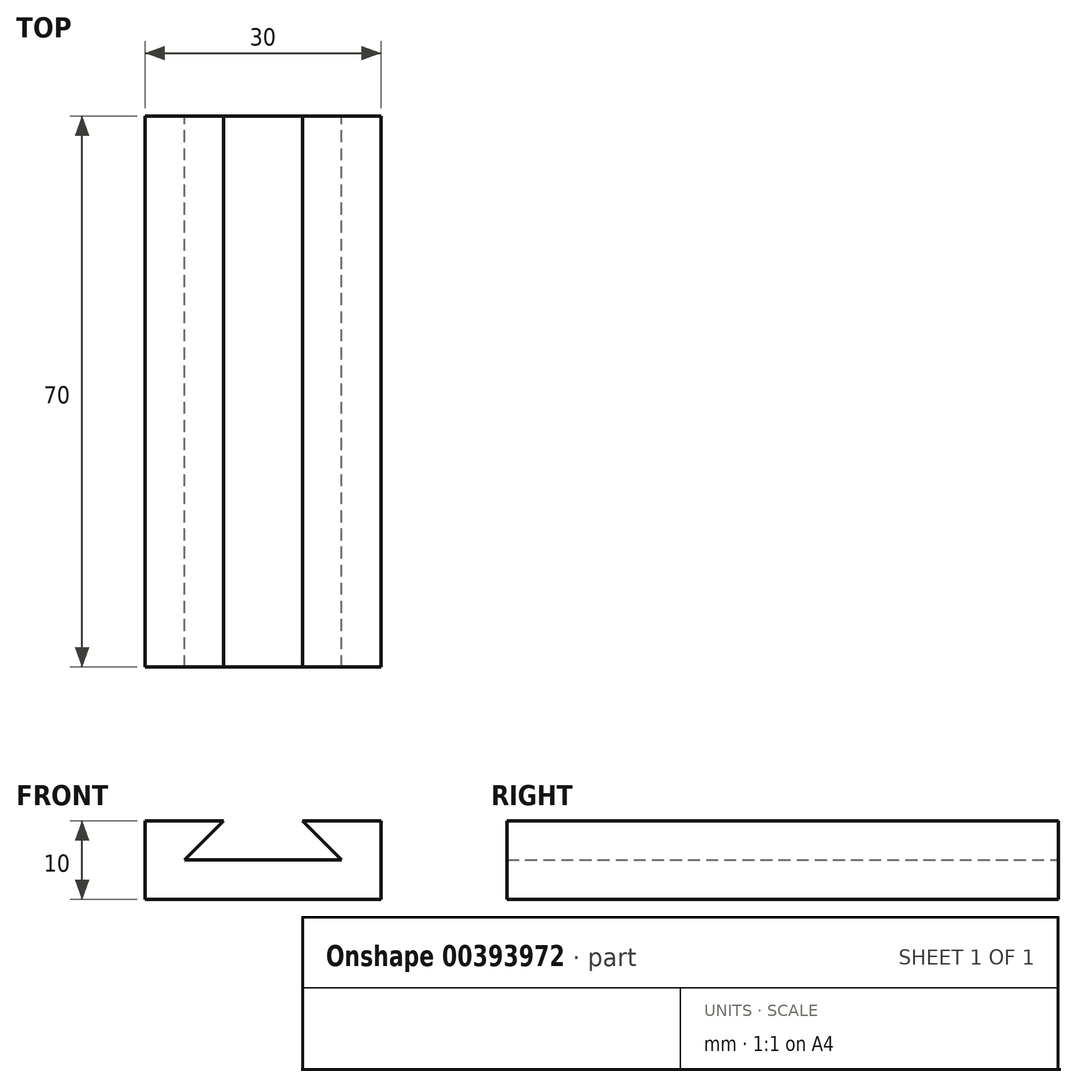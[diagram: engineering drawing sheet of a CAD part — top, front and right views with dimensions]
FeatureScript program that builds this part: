
annotation { "Feature Type Name" : "Feature", "Feature Type Description" : "" }
export const myFeature = defineFeature(function(context is Context, id is Id, definition is map)
    precondition{}
    {
        {
            var Q0;
            Q0=qCreatedBy(makeId("Front.planeOp"),FACE);
            var sketch = newSketch(context, id + "F0", { "sketchPlane" : qUnion([Q0])});
            skLineSegment(sketch, "E0.bottom", {"start": v(0, 0) * mm, "end": v(30, 0) * mm});
            skLineSegment(sketch, "E0.top", {"start": v(0, 10) * mm, "end": v(30, 10) * mm});
            skLineSegment(sketch, "E0.left", {"start": v(0, 0) * mm, "end": v(0, 10) * mm});
            skLineSegment(sketch, "E0.right", {"start": v(30, 0) * mm, "end": v(30, 10) * mm});
            skLineSegment(sketch, "E1", {"start": v(10, 10) * mm, "end": v(5, 5) * mm});
            skLineSegment(sketch, "E2", {"start": v(5, 5) * mm, "end": v(20, 5) * mm});
            skLineSegment(sketch, "E3", {"start": v(20, 5) * mm, "end": v(20, 10) * mm});
            skLineSegment(sketch, "E4", {"start": v(15, 5) * mm, "end": v(15, 10) * mm});
            skPoint(sketch, "E4.startSnap0", {"position": v(15, 0) * mm});
            skLineSegment(sketch, "E5.MirrorCS", {"start": v(20, 10) * mm, "end": v(25, 5) * mm});
            skLineSegment(sketch, "E6", {"start": v(20, 5) * mm, "end": v(25, 5) * mm});
            skSolve(sketch);
        }
        {
            var Q0;
            Q0=makeQuery(id+"F0.imprint","IMPRINT",FACE,{"disambiguationData":[TD([[makeQuery(id+"F0.imprint","IMPRINT",EDGE,{"derivedFrom":sQuery(id+"F0.wireOp",EDGE,"E0.bottom")}),1.0]])]});
            extrude(context, id + "F1", {"entities" : qUnion([Q0]), "depth" : 70 * mm});
        }
    });
